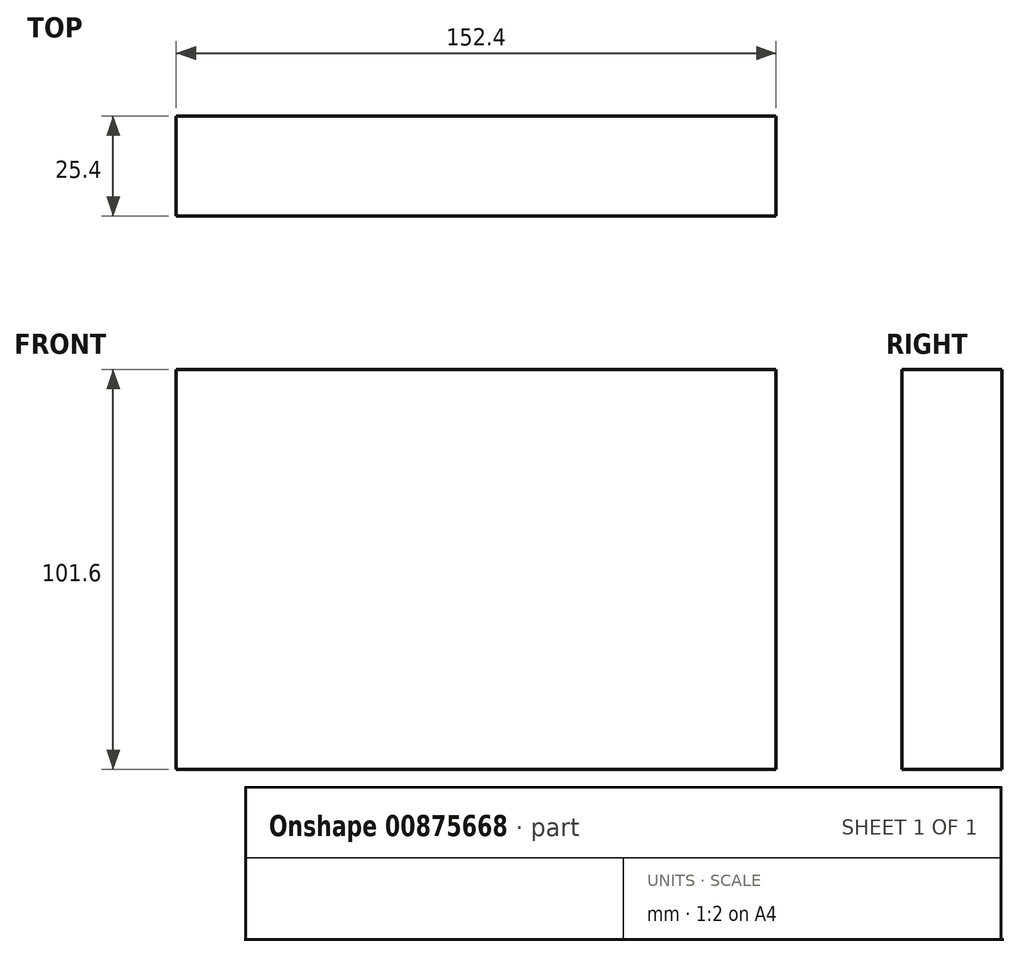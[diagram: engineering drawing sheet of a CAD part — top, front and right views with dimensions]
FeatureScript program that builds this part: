
annotation { "Feature Type Name" : "Feature", "Feature Type Description" : "" }
export const myFeature = defineFeature(function(context is Context, id is Id, definition is map)
    precondition{}
    {
        {
            var Q0;
            Q0=qCreatedBy(makeId("Front.planeOp"),FACE);
            var sketch = newSketch(context, id + "F0", { "sketchPlane" : qUnion([Q0])});
            skLineSegment(sketch, "E0", {"start": v(-76.2, 50.8) * mm, "end": v(-76.2, -50.8) * mm});
            skLineSegment(sketch, "E1", {"start": v(-76.2, -50.8) * mm, "end": v(76.2, -50.8) * mm});
            skLineSegment(sketch, "E2", {"start": v(76.2, -50.8) * mm, "end": v(76.2, 50.8) * mm});
            skLineSegment(sketch, "E3", {"start": v(76.2, 50.8) * mm, "end": v(-76.2, 50.8) * mm});
            skSolve(sketch);
        }
        {
            var Q0;
            Q0 = qSketchRegion(id + "F0", true);
            extrude(context, id + "F1", {"entities" : qUnion([Q0]), "depth" : 25.4 * mm, "offsetDistance" : 25.4 * mm});
        }
    });
